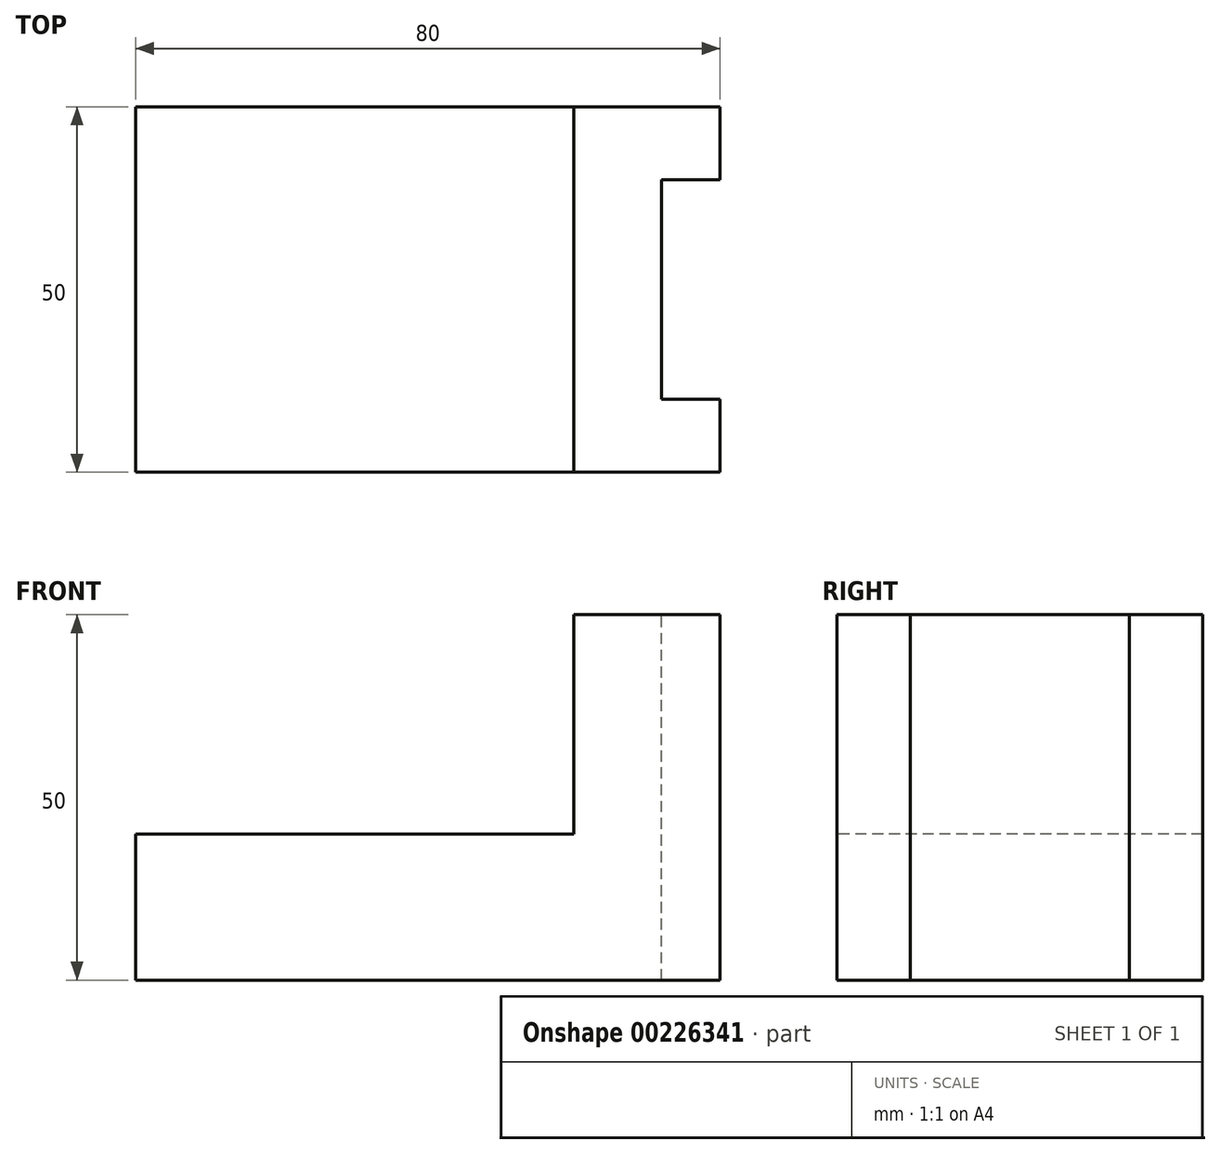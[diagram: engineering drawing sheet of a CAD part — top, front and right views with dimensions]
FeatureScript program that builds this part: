
annotation { "Feature Type Name" : "Feature", "Feature Type Description" : "" }
export const myFeature = defineFeature(function(context is Context, id is Id, definition is map)
    precondition{}
    {
        {
            var Q0;
            Q0=qCreatedBy(makeId("Top.planeOp"),FACE);
            var sketch = newSketch(context, id + "F0", { "sketchPlane" : qUnion([Q0])});
            skLineSegment(sketch, "E0.bottom", {"start": v(40, 25) * mm, "end": v(-40, 25) * mm});
            skLineSegment(sketch, "E0.top", {"start": v(40, -25) * mm, "end": v(-40, -25) * mm});
            skLineSegment(sketch, "E0.left", {"start": v(40, 25) * mm, "end": v(40, -25) * mm});
            skLineSegment(sketch, "E0.right", {"start": v(-40, 25) * mm, "end": v(-40, -25) * mm});
            skPoint(sketch, "E0.middle", {"position": v(0, 0) * mm});
            skSolve(sketch);
        }
        {
            var Q0;
            Q0=makeQuery(id+"F0.imprint","IMPRINT",FACE,{"disambiguationData":[TD([[makeQuery(id+"F0.imprint","IMPRINT",EDGE,{"derivedFrom":sQuery(id+"F0.wireOp",EDGE,"E0.bottom")}),1.0]])]});
            extrude(context, id + "F1", {"entities" : qUnion([Q0]), "depth" : 20 * mm});
        }
        {
            var Q0;
            Q0=makeQuery(id+"F1.opExtrude","CAP_FACE",FACE,{"disambiguationData":[OSD([sQuery(id+"F0.wireOp",EDGE,"E0.bottom"),sQuery(id+"F0.wireOp",EDGE,"E0.top"),sQuery(id+"F0.wireOp",EDGE,"E0.left"),sQuery(id+"F0.wireOp",EDGE,"E0.right")])],"isStart":false});
            var sketch = newSketch(context, id + "F2", { "sketchPlane" : qUnion([Q0])});
            skLineSegment(sketch, "E1.bottom", {"start": v(40, 25) * mm, "end": v(20, 25) * mm});
            skLineSegment(sketch, "E1.top", {"start": v(40, -25) * mm, "end": v(20, -25) * mm});
            skLineSegment(sketch, "E1.left", {"start": v(40, 25) * mm, "end": v(40, -25) * mm});
            skLineSegment(sketch, "E1.right", {"start": v(20, 25) * mm, "end": v(20, -25) * mm});
            skSolve(sketch);
        }
        {
            var Q0;
            Q0=makeQuery(id+"F2.imprint","IMPRINT",FACE,{"disambiguationData":[TD([[makeQuery(id+"F2.imprint","IMPRINT",EDGE,{"derivedFrom":sQuery(id+"F2.wireOp",EDGE,"E1.bottom")}),1.0]])]});
            extrude(context, id + "F3", {"entities" : qUnion([Q0]), "operationType" : NewBodyOperationType.ADD, "depth" : 30 * mm});
        }
        {
            var Q0;
            Q0=makeQuery(id+"F3.opExtrude","CAP_FACE",FACE,{"disambiguationData":[OSD([sQuery(id+"F2.wireOp",EDGE,"E1.bottom"),sQuery(id+"F2.wireOp",EDGE,"E1.top"),sQuery(id+"F2.wireOp",EDGE,"E1.left"),sQuery(id+"F2.wireOp",EDGE,"E1.right")])],"isStart":false});
            var sketch = newSketch(context, id + "F4", { "sketchPlane" : qUnion([Q0])});
            skLineSegment(sketch, "E2.bottom", {"start": v(40, 15) * mm, "end": v(32, 15) * mm});
            skLineSegment(sketch, "E2.top", {"start": v(40, -15) * mm, "end": v(32, -15) * mm});
            skLineSegment(sketch, "E2.left", {"start": v(40, 15) * mm, "end": v(40, -15) * mm});
            skLineSegment(sketch, "E2.right", {"start": v(32, 15) * mm, "end": v(32, -15) * mm});
            skSolve(sketch);
        }
        {
            var Q0;
            Q0=makeQuery(id+"F4.imprint","IMPRINT",FACE,{"disambiguationData":[TD([[makeQuery(id+"F4.imprint","IMPRINT",EDGE,{"derivedFrom":sQuery(id+"F4.wireOp",EDGE,"E2.bottom")}),1.0]])]});
            extrude(context, id + "F5", {"entities" : qUnion([Q0]), "operationType" : NewBodyOperationType.REMOVE, "endBound" : BoundingType.THROUGH_ALL, "oppositeDirection" : true, "depth" : 25 * mm});
        }
    });
